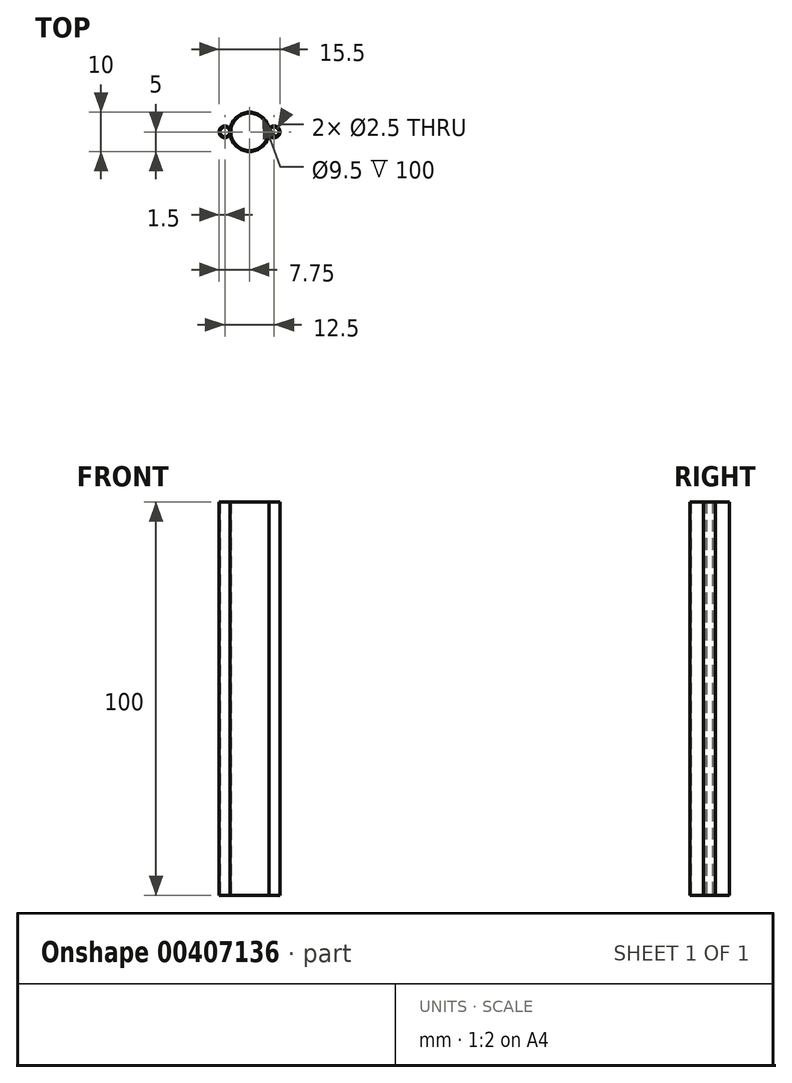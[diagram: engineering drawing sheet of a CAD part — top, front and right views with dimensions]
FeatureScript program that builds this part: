
annotation { "Feature Type Name" : "Feature", "Feature Type Description" : "" }
export const myFeature = defineFeature(function(context is Context, id is Id, definition is map)
    precondition{}
    {
        {
            var Q0;
            Q0=qCreatedBy(makeId("Top.planeOp"),FACE);
            var sketch = newSketch(context, id + "F0", { "sketchPlane" : qUnion([Q0])});
            skCircle(sketch, "E0", {"center": v(0, 0) * mm, "radius": 5 * mm});
            skCircle(sketch, "E1", {"center": v(0, 0) * mm, "radius": 4.75 * mm});
            skSolve(sketch);
        }
        {
            var Q0;
            Q0=qSketchRegion(id+"F0",true);
            extrude(context, id + "F1", {"entities" : qUnion([Q0]), "depth" : 100 * mm});
        }
        {
            var Q0;
            Q0=qCreatedBy(makeId("Top.planeOp"),FACE);
            var sketch = newSketch(context, id + "F2", { "sketchPlane" : qUnion([Q0])});
            skLineSegment(sketch, "E2", {"start": v(0, 3.57) * mm, "end": v(0, -3.32) * mm, "construction": true});
            skCircle(sketch, "E3", {"center": v(-6.25, 0) * mm, "radius": 1.25 * mm});
            skCircle(sketch, "E4", {"center": v(6.25, 0) * mm, "radius": 1.5 * mm});
            skCircle(sketch, "E5", {"center": v(6.25, 0) * mm, "radius": 1.25 * mm});
            skCircle(sketch, "E6", {"center": v(-6.25, 0) * mm, "radius": 1.5 * mm});
            skSolve(sketch);
        }
        {
            var Q0;
            Q0 = qSketchRegion(id + "F2", true);
            var Q1;
            Q1=makeQuery(id+"F1.opExtrude","CAP_FACE",FACE,{"disambiguationData":[OSD([sQuery(id+"F0.wireOp",EDGE,"E0"),sQuery(id+"F0.wireOp",EDGE,"E1")])],"isStart":false});
            extrude(context, id + "F3", {"entities" : qUnion([Q0]), "operationType" : NewBodyOperationType.ADD, "endBound" : BoundingType.UP_TO_SURFACE, "depth" : 25 * mm, "endBoundEntityFace" : qUnion([Q1]), "offsetDistance" : 25 * mm});
        }
    });
